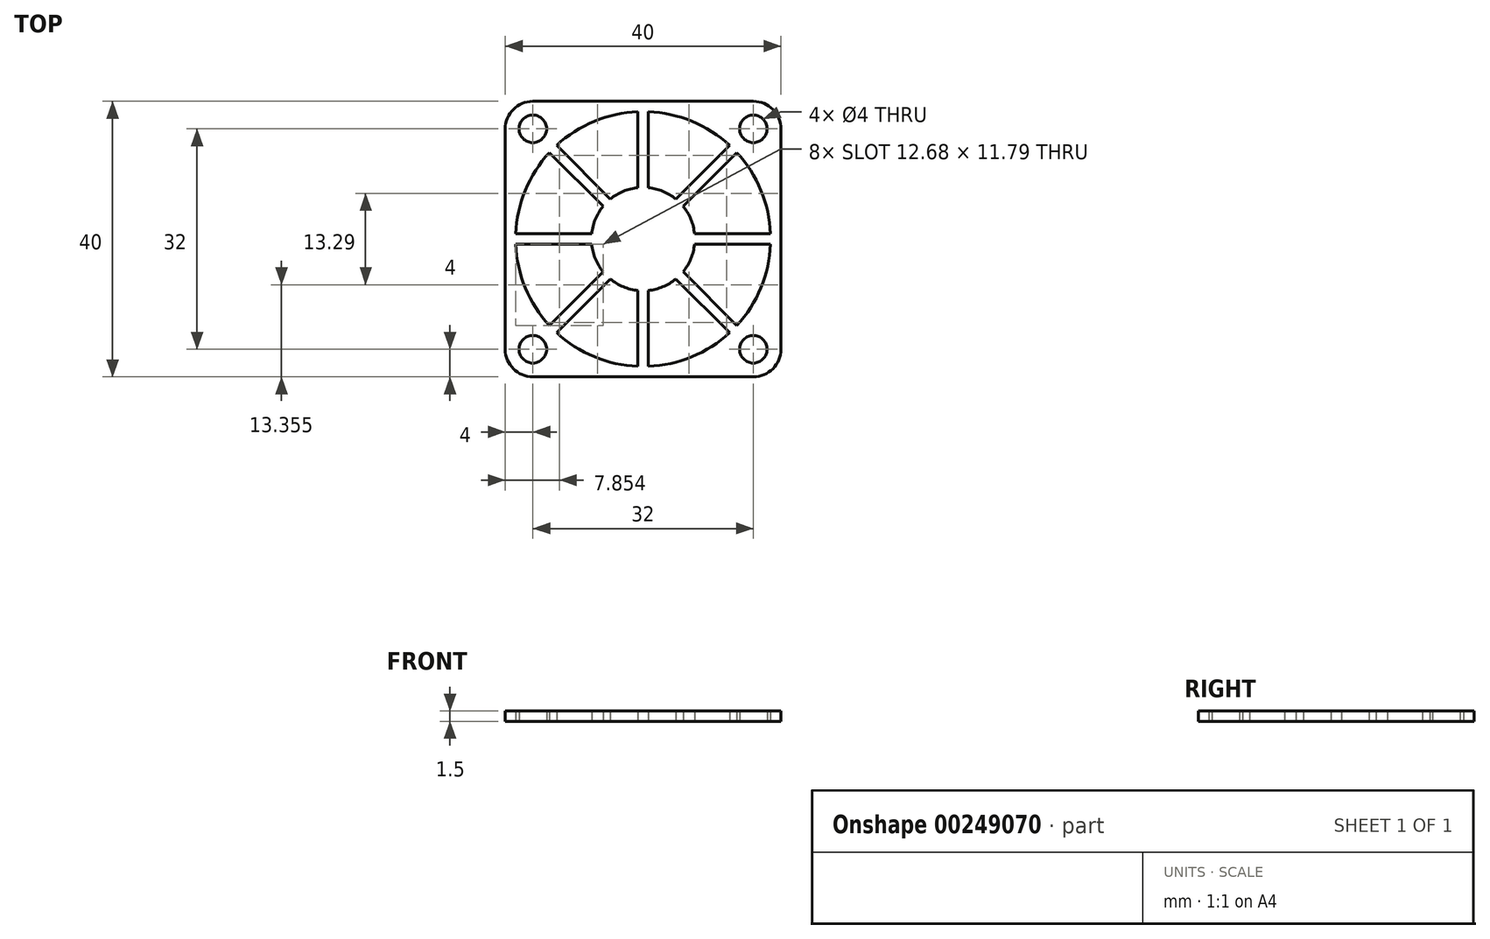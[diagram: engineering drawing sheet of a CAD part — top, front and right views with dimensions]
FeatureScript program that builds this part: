
annotation { "Feature Type Name" : "Feature", "Feature Type Description" : "" }
export const myFeature = defineFeature(function(context is Context, id is Id, definition is map)
    precondition{}
    {
        {
            var Q0;
            Q0=qCreatedBy(makeId("Top.planeOp"),FACE);
            var sketch = newSketch(context, id + "F0", { "sketchPlane" : qUnion([Q0])});
            skLineSegment(sketch, "E0.bottom", {"start": v(-20, 20) * mm, "end": v(20, 20) * mm});
            skLineSegment(sketch, "E0.top", {"start": v(-20, -20) * mm, "end": v(20, -20) * mm});
            skLineSegment(sketch, "E0.left", {"start": v(-20, 20) * mm, "end": v(-20, -20) * mm});
            skLineSegment(sketch, "E0.right", {"start": v(20, 20) * mm, "end": v(20, -20) * mm});
            skCircle(sketch, "E1", {"center": v(16, 16) * mm, "radius": 2 * mm});
            skCircle(sketch, "E2", {"center": v(-16, 16) * mm, "radius": 2 * mm});
            skCircle(sketch, "E3", {"center": v(-16, -16) * mm, "radius": 2 * mm});
            skCircle(sketch, "E4", {"center": v(16, -16) * mm, "radius": 2 * mm});
            skSolve(sketch);
        }
        {
            var Q0;
            Q0 = qSketchRegion(id + "F0", true);
            extrude(context, id + "F1", {"entities" : qUnion([Q0]), "depth" : 1.5 * mm});
        }
        {
            var Q0;
            Q0=qCreatedBy(makeId("Top.planeOp"),FACE);
            var sketch = newSketch(context, id + "F2", { "sketchPlane" : qUnion([Q0])});
            skLineSegment(sketch, "E5.0", {"start": v(-20, 20) * mm, "end": v(20, 20) * mm});
            skLineSegment(sketch, "E6.0", {"start": v(-20, 20) * mm, "end": v(-20, -20) * mm});
            skLineSegment(sketch, "E7.0", {"start": v(-20, -20) * mm, "end": v(20, -20) * mm});
            skLineSegment(sketch, "E8.0", {"start": v(20, 20) * mm, "end": v(20, -20) * mm});
            skLineSegment(sketch, "E9", {"start": v(0, 7.5) * mm, "end": v(0, 18.5) * mm, "construction": true});
            skLineSegment(sketch, "E10", {"start": v(-0.75, 18.48) * mm, "end": v(-0.75, 7.46) * mm});
            skLineSegment(sketch, "E11.MirrorCS", {"start": v(0.75, 18.48) * mm, "end": v(0.75, 7.46) * mm});
            skArc(sketch, "E12", {"start": v(-0.75, 18.48) * mm, "mid": v(-7.08, 17.1) * mm, "end": v(-12.54, 13.6) * mm});
            skArc(sketch, "E13", {"start": v(-0.75, 7.46) * mm, "mid": v(-2.87, 6.93) * mm, "end": v(-4.75, 5.8) * mm});
            skLineSegment(sketch, "E14.1.0", {"start": v(-13.6, 12.54) * mm, "end": v(-5.8, 4.75) * mm});
            skLineSegment(sketch, "E14.1.1", {"start": v(-12.54, 13.6) * mm, "end": v(-4.75, 5.8) * mm});
            skLineSegment(sketch, "E14.2.0", {"start": v(-18.48, -0.75) * mm, "end": v(-7.46, -0.75) * mm});
            skLineSegment(sketch, "E14.2.1", {"start": v(-18.48, 0.75) * mm, "end": v(-7.46, 0.75) * mm});
            skLineSegment(sketch, "E14.3.0", {"start": v(-12.54, -13.6) * mm, "end": v(-4.75, -5.8) * mm});
            skLineSegment(sketch, "E14.3.1", {"start": v(-13.6, -12.54) * mm, "end": v(-5.8, -4.75) * mm});
            skLineSegment(sketch, "E14.4.0", {"start": v(0.75, -18.48) * mm, "end": v(0.75, -7.46) * mm});
            skLineSegment(sketch, "E14.4.1", {"start": v(-0.75, -18.48) * mm, "end": v(-0.75, -7.46) * mm});
            skLineSegment(sketch, "E14.5.0", {"start": v(13.6, -12.54) * mm, "end": v(5.8, -4.75) * mm});
            skLineSegment(sketch, "E14.5.1", {"start": v(12.54, -13.6) * mm, "end": v(4.75, -5.8) * mm});
            skLineSegment(sketch, "E14.6.0", {"start": v(18.48, 0.75) * mm, "end": v(7.46, 0.75) * mm});
            skLineSegment(sketch, "E14.6.1", {"start": v(18.48, -0.75) * mm, "end": v(7.46, -0.75) * mm});
            skLineSegment(sketch, "E14.7.0", {"start": v(12.54, 13.6) * mm, "end": v(4.75, 5.8) * mm});
            skLineSegment(sketch, "E14.7.1", {"start": v(13.6, 12.54) * mm, "end": v(5.8, 4.75) * mm});
            skArc(sketch, "E15.trimOffspring", {"start": v(-5.8, 4.75) * mm, "mid": v(-2.87, -6.93) * mm, "end": v(7.46, -0.75) * mm});
            skArc(sketch, "E16.trimOffspring", {"start": v(-13.6, 12.54) * mm, "mid": v(-17.1, 7.08) * mm, "end": v(-18.48, 0.75) * mm});
            skArc(sketch, "E17.trimOffspring", {"start": v(4.75, 5.8) * mm, "mid": v(2.87, 6.93) * mm, "end": v(0.75, 7.46) * mm});
            skArc(sketch, "E18.trimOffspring", {"start": v(12.54, 13.6) * mm, "mid": v(7.08, 17.1) * mm, "end": v(0.75, 18.48) * mm});
            skArc(sketch, "E19.trimOffspring", {"start": v(18.48, 0.75) * mm, "mid": v(17.1, 7.08) * mm, "end": v(13.6, 12.54) * mm});
            skArc(sketch, "E20.trimOffspring", {"start": v(7.46, 0.75) * mm, "mid": v(6.93, 2.87) * mm, "end": v(5.8, 4.75) * mm});
            skArc(sketch, "E21.trimOffspring", {"start": v(13.6, -12.54) * mm, "mid": v(17.1, -7.08) * mm, "end": v(18.48, -0.75) * mm});
            skArc(sketch, "E22.trimOffspring", {"start": v(0.75, -18.48) * mm, "mid": v(7.08, -17.1) * mm, "end": v(12.54, -13.6) * mm});
            skArc(sketch, "E23.trimOffspring", {"start": v(-12.54, -13.6) * mm, "mid": v(-7.08, -17.1) * mm, "end": v(-0.75, -18.48) * mm});
            skArc(sketch, "E24.trimOffspring", {"start": v(-18.48, -0.75) * mm, "mid": v(-17.1, -7.08) * mm, "end": v(-13.6, -12.54) * mm});
            skSolve(sketch);
        }
        {
            var Q0;
            Q0 = qSketchRegion(id + "F2", true);
            extrude(context, id + "F3", {"entities" : qUnion([Q0]), "operationType" : NewBodyOperationType.INTERSECT, "depth" : 25 * mm});
        }
        {
            var Q0;
            Q0=makeQuery(id+"F1.opExtrude","SWEPT_EDGE",EDGE,{"disambiguationData":[OSD([sQuery(id+"F0.wireOp",EDGE,"E0.bottom"),sQuery(id+"F0.wireOp",EDGE,"E0.left")])]});
            var Q1;
            Q1=makeQuery(id+"F1.opExtrude","SWEPT_EDGE",EDGE,{"disambiguationData":[OSD([sQuery(id+"F0.wireOp",EDGE,"E0.bottom"),sQuery(id+"F0.wireOp",EDGE,"E0.right")])]});
            var Q2;
            Q2=makeQuery(id+"F1.opExtrude","SWEPT_EDGE",EDGE,{"disambiguationData":[OSD([sQuery(id+"F0.wireOp",EDGE,"E0.top"),sQuery(id+"F0.wireOp",EDGE,"E0.left")])]});
            var Q3;
            Q3=makeQuery(id+"F1.opExtrude","SWEPT_EDGE",EDGE,{"disambiguationData":[OSD([sQuery(id+"F0.wireOp",EDGE,"E0.top"),sQuery(id+"F0.wireOp",EDGE,"E0.right")])]});
            fillet(context, id + "F4", {"entities" : qUnion([Q0, Q1, Q2, Q3]), "radius" : 4 * mm, "tangentPropagation" : true, "allowEdgeOverflow" : false});
        }
    });
